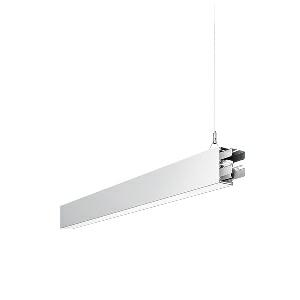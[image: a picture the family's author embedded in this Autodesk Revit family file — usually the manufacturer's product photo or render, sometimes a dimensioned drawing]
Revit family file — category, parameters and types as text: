
# Revit family: idoo_line_-_ilp_3000_vtl_d_mid_00806450_96f0
name_source: partatom
category: Lighting Fixtures
units: mm (PartAtom-declared; Revit-internal decimal feet)

## family parameters
Cut with Voids When Loaded = No
Host = Face
Light Source = No
Part Type = Normal
Room Calculation Point = No
Round Connector Dimension = Use Diameter
Shared = No

## types (1)
- IDOO.line - ILP 3000/VTL/D MID (1 x LED, 3150 lm, 2700-6500K)
    Apparent Load = 32 VA
    Approval mark = CE
    CIE Flux Codes = 66 91 98 40 100
    Color Rendering = 90-100
    Color Temperature = 2700-6500K
    Control Gear = Electronic ballast
    Default Elevation = 1800 mm
    Description = ILP 3000/VTL/D|Suspended luminaire|light source: LED|connected load: 220-240 V, 50/60 Hz|Power consumption: approx. 32 W|standby: approx. 0,25|luminous flux: 3150 lm|luminous efficacy: 98 lm/W|light distribution: Direct/indirect|direct ratio: approx. 40 %|colour temperature: Cold white, ca. 2700-6500 K|color rendering index (CRI): >= 90|chromaticity tolerance:  3 SDCM|System of protection: IP 40|technology: Continuously dimmable|luminaire body|material: Sectional aluminium|colour: White|lamp cover: Acrylic (PMMA), Clear|mains lead: 1,0 m With free stranded wires|Fastening: Steel cable 0.3 - 0.7 m|glare control: Prism aperture|luminance(L65): <= 2700 cd/m|unified glare rating(4H 8H): <=  16|special features: Specified values at approx. 4000 K, DALI Load 1x, Through-wired, up to 18 m on one mains connection, External control required for Dali Device type 8, Flicker-free, Constant luminous flux between 2700 and 6500 K, Constant colour temperature over the whole dimming range, Mechanical and electrical connection of the individual modules without tools|
    Frequency = 50 Hz
    Height = 110 mm
    Lamp = 1 x LED
    Lamp Light Flux = 3150 lm
    Lamp count = 1
    Length = 1122 mm
    Luminous efficacy = 98 lm/W
    Manufacturer = Waldmann
    ModVariant = No
    Model = 00806450
    Mounting Place = Ceiling
    Mounting Type = Pendant
    Number of Poles = 1
    OnlyDefault = Yes
    Power Factor = 1
    Product Name = IDOO.line - ILP 3000/VTL/D MID
    Product group = Suspended luminaire
    ProductGroupID = 9
    Protection Class = Protection class I
    Protection Degree = IP 40
    RLX_Detail_Level = 1
    RLX_Emergency_Light_Flux = 0 lm
    RLX_Emergency_Type = 0
    RLX_Emergency_Type_DB = No
    RlxData = <blob elided: 19565 chars, md5=0e849f10>
    Socket = socket
    Standby Power = 0 W
    System Light Flux = 3150 lm
    System Power = 32 W
    Type Comments = Product without accessories
    Type Image = 113302000-00692570.jpg
    URL = http://relux.com
    VarID = ---
    Voltage = 230 V
    Voltage Range = 220-240 V
    Weight = 0.00 kg
    Width = 60 mm  [stored 0.19685 ft]

note: [stored X ft] marks values corroborated as IEEE doubles in the binary element streams (Revit-internal decimal feet)

## geometry (parser evidence)
native form markers: Blend x4, Sweep x14
no freeform markers — native parametric forms only
